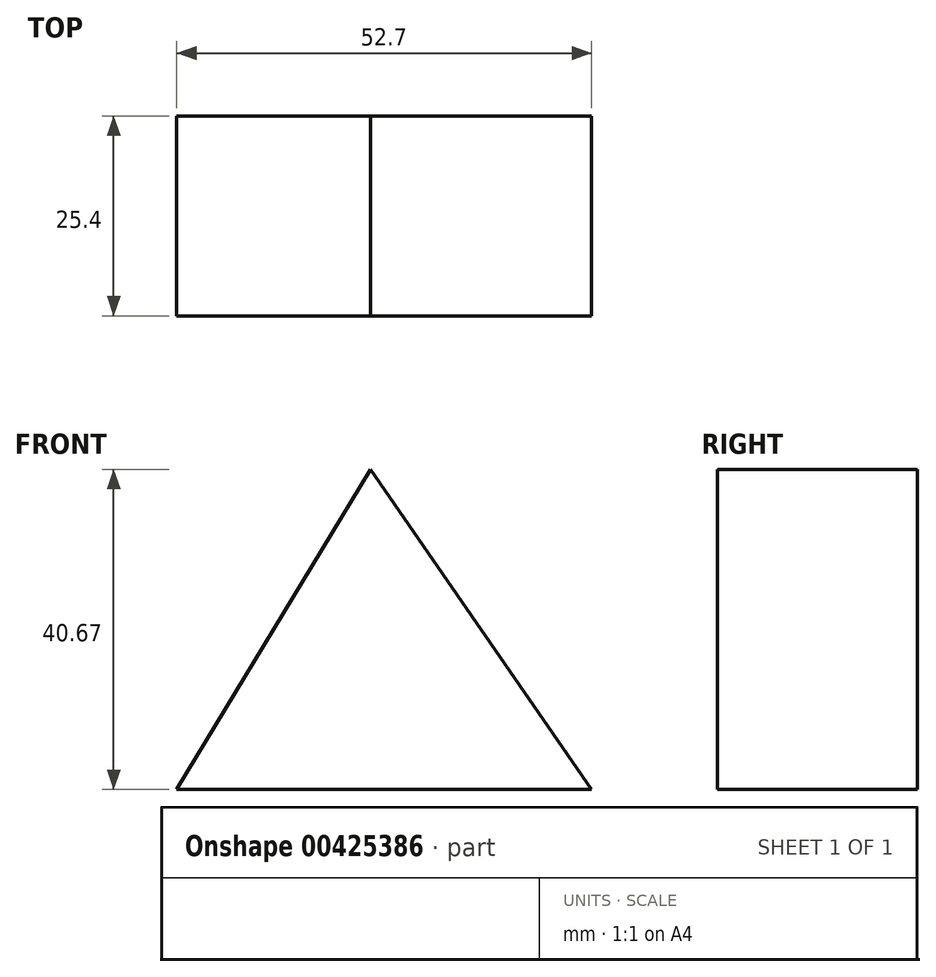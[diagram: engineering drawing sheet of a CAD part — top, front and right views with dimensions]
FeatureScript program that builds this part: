
annotation { "Feature Type Name" : "Feature", "Feature Type Description" : "" }
export const myFeature = defineFeature(function(context is Context, id is Id, definition is map)
    precondition{}
    {
        {
            var Q0;
            Q0=qCreatedBy(makeId("Front.planeOp"),FACE);
            var sketch = newSketch(context, id + "F0", { "sketchPlane" : qUnion([Q0])});
            skLineSegment(sketch, "E0", {"start": v(0, 0) * mm, "end": v(-52.7, 0) * mm});
            skLineSegment(sketch, "E1", {"start": v(-52.7, 0) * mm, "end": v(-28.07, 40.67) * mm});
            skLineSegment(sketch, "E2", {"start": v(-28.07, 40.67) * mm, "end": v(0, 0) * mm});
            skSolve(sketch);
        }
        {
            var Q0;
            Q0=makeQuery(id+"F0.imprint","IMPRINT",FACE,{"disambiguationData":[TD([[makeQuery(id+"F0.imprint","IMPRINT",EDGE,{"derivedFrom":sQuery(id+"F0.wireOp",EDGE,"E0")}),-1.0]])]});
            extrude(context, id + "F1", {"entities" : qUnion([Q0]), "depth" : 25.4 * mm});
        }
    });
